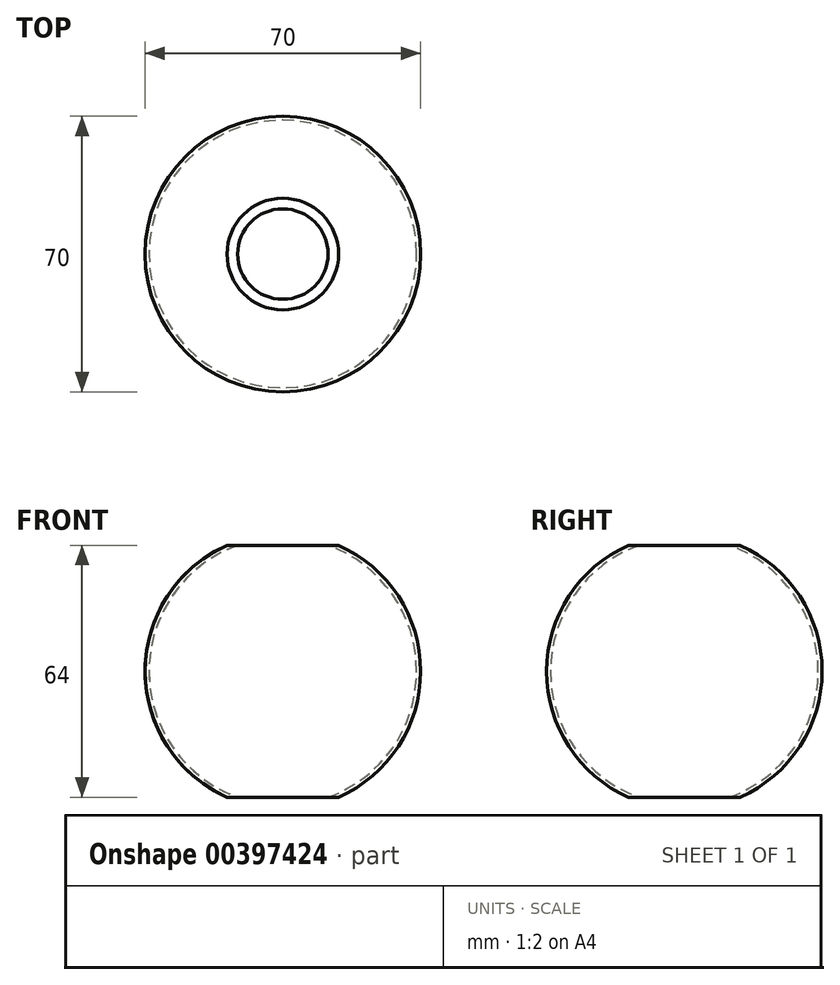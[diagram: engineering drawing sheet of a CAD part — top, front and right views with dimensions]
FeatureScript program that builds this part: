
annotation { "Feature Type Name" : "Feature", "Feature Type Description" : "" }
export const myFeature = defineFeature(function(context is Context, id is Id, definition is map)
    precondition{}
    {
        {
            var Q0;
            Q0=qCreatedBy(makeId("Right.planeOp"),FACE);
            var sketch = newSketch(context, id + "F0", { "sketchPlane" : qUnion([Q0])});
            skArc(sketch, "E0", {"start": v(-14.18, 32) * mm, "mid": v(-35, 0) * mm, "end": v(-14.18, -32) * mm});
            skArc(sketch, "E1", {"start": v(-11.49, 32) * mm, "mid": v(-34, 0) * mm, "end": v(-11.49, -32) * mm});
            skLineSegment(sketch, "E2", {"start": v(-11.49, 32) * mm, "end": v(-14.18, 32) * mm});
            skLineSegment(sketch, "E3", {"start": v(-11.49, -32) * mm, "end": v(-14.18, -32) * mm});
            skSolve(sketch);
        }
        {
            var Q0;
            Q0=qCreatedBy(makeId("Right.planeOp"),FACE);
            var sketch = newSketch(context, id + "F1", { "sketchPlane" : qUnion([Q0])});
            skLineSegment(sketch, "E4", {"start": v(0, 0) * mm, "end": v(0, 10) * mm});
            skSolve(sketch);
        }
        {
            var Q0;
            Q0 = qSketchRegion(id + "F0", true);
            var Q1;
            Q1=sQuery(id+"F1.wireOp",EDGE,"E4");
            revolve(context, id + "F2", {"entities" : qUnion([Q0]), "axis" : qUnion([Q1]), "revolveType" : RevolveType.FULL});
        }
    });
